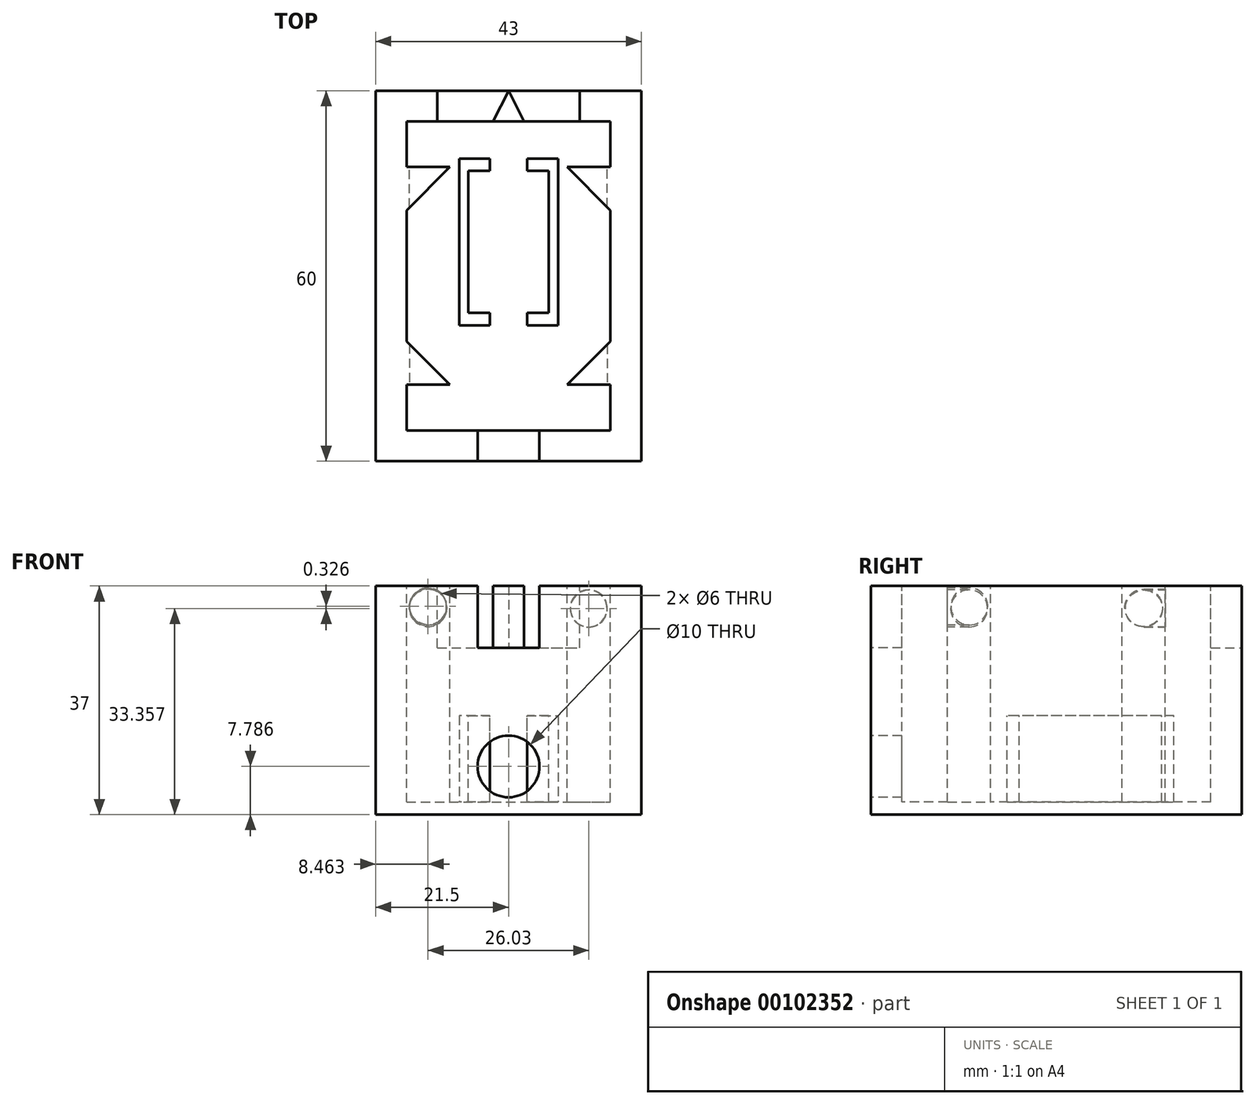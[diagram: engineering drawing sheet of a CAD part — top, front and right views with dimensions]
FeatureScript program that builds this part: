
annotation { "Feature Type Name" : "Feature", "Feature Type Description" : "" }
export const myFeature = defineFeature(function(context is Context, id is Id, definition is map)
    precondition{}
    {
        {
            var Q0;
            Q0=qCreatedBy(makeId("Top.planeOp"),FACE);
            var sketch = newSketch(context, id + "F0", { "sketchPlane" : qUnion([Q0])});
            skLineSegment(sketch, "E0.bottom", {"start": v(-21.5, 30) * mm, "end": v(21.5, 30) * mm});
            skLineSegment(sketch, "E0.top", {"start": v(-21.5, -30) * mm, "end": v(21.5, -30) * mm});
            skLineSegment(sketch, "E0.left", {"start": v(-21.5, 30) * mm, "end": v(-21.5, -30) * mm});
            skLineSegment(sketch, "E0.right", {"start": v(21.5, 30) * mm, "end": v(21.5, -30) * mm});
            skPoint(sketch, "E0.middle", {"position": v(0, 0) * mm});
            skSolve(sketch);
        }
        {
            var Q0;
            Q0=makeQuery(id+"F0.imprint","IMPRINT",FACE,{"disambiguationData":[TD([[makeQuery(id+"F0.imprint","IMPRINT",EDGE,{"derivedFrom":sQuery(id+"F0.wireOp",EDGE,"E0.bottom")}),-1.0]])]});
            extrude(context, id + "F1", {"entities" : qUnion([Q0]), "depth" : 37 * mm});
        }
        {
            var Q0;
            Q0=makeQuery(id+"F1.opExtrude","CAP_FACE",FACE,{"disambiguationData":[OSD([sQuery(id+"F0.wireOp",EDGE,"E0.bottom"),sQuery(id+"F0.wireOp",EDGE,"E0.top"),sQuery(id+"F0.wireOp",EDGE,"E0.left"),sQuery(id+"F0.wireOp",EDGE,"E0.right")])],"isStart":false});
            var sketch = newSketch(context, id + "F2", { "sketchPlane" : qUnion([Q0])});
            skLineSegment(sketch, "E1.bottom", {"start": v(-16.5, 25) * mm, "end": v(16.5, 25) * mm});
            skLineSegment(sketch, "E1.top", {"start": v(-16.5, -25) * mm, "end": v(16.5, -25) * mm});
            skLineSegment(sketch, "E1.left", {"start": v(-16.5, 25) * mm, "end": v(-16.5, -25) * mm});
            skLineSegment(sketch, "E1.right", {"start": v(16.5, 25) * mm, "end": v(16.5, -25) * mm});
            skPoint(sketch, "E1.middle", {"position": v(0, 0) * mm});
            skSolve(sketch);
        }
        {
            var Q0;
            Q0 = qSketchRegion(id + "F2", true);
            extrude(context, id + "F3", {"entities" : qUnion([Q0]), "operationType" : NewBodyOperationType.REMOVE, "oppositeDirection" : true, "depth" : 35 * mm});
        }
        {
            var Q0;
            Q0=makeQuery(id+"F1.opExtrude","CAP_FACE",FACE,{"disambiguationData":[OSD([sQuery(id+"F0.wireOp",EDGE,"E0.bottom"),sQuery(id+"F0.wireOp",EDGE,"E0.top"),sQuery(id+"F0.wireOp",EDGE,"E0.left"),sQuery(id+"F0.wireOp",EDGE,"E0.right")])],"isStart":false});
            var sketch = newSketch(context, id + "F4", { "sketchPlane" : qUnion([Q0])});
            skLineSegment(sketch, "E2", {"start": v(0, 30) * mm, "end": v(-11.5, 30) * mm});
            skLineSegment(sketch, "E3", {"start": v(-11.5, 30) * mm, "end": v(-11.5, 25) * mm});
            skLineSegment(sketch, "E4", {"start": v(-11.5, 25) * mm, "end": v(0, 25) * mm});
            skLineSegment(sketch, "E5", {"start": v(0, 25) * mm, "end": v(11.5, 25) * mm});
            skLineSegment(sketch, "E6", {"start": v(11.5, 25) * mm, "end": v(11.5, 30) * mm});
            skLineSegment(sketch, "E7", {"start": v(11.5, 30) * mm, "end": v(0, 30) * mm});
            skSolve(sketch);
        }
        {
            var Q0;
            Q0 = qSketchRegion(id + "F4", true);
            extrude(context, id + "F5", {"entities" : qUnion([Q0]), "operationType" : NewBodyOperationType.REMOVE, "oppositeDirection" : true, "depth" : 10 * mm});
        }
        {
            var Q0;
            Q0=makeQuery(id+"F5.boolean.opBoolean","COPY",FACE,{"derivedFrom":makeQuery(id+"F5.opExtrude","CAP_FACE",FACE,{"disambiguationData":[OSD([sQuery(id+"F4.wireOp",EDGE,"E2"),sQuery(id+"F4.wireOp",EDGE,"E3"),sQuery(id+"F4.wireOp",EDGE,"E4"),sQuery(id+"F4.wireOp",EDGE,"E5"),sQuery(id+"F4.wireOp",EDGE,"E6"),sQuery(id+"F4.wireOp",EDGE,"E7")])],"isStart":false})});
            var sketch = newSketch(context, id + "F6", { "sketchPlane" : qUnion([Q0])});
            skLineSegment(sketch, "E8", {"start": v(0, 30) * mm, "end": v(-2.5, 25) * mm});
            skLineSegment(sketch, "E9", {"start": v(-2.5, 25) * mm, "end": v(0, 25) * mm});
            skLineSegment(sketch, "E10", {"start": v(0, 25) * mm, "end": v(2.5, 25) * mm});
            skLineSegment(sketch, "E11", {"start": v(2.5, 25) * mm, "end": v(0, 30) * mm});
            skSolve(sketch);
        }
        {
            var Q0;
            Q0=makeQuery(id+"F6.imprint","IMPRINT",FACE,{"disambiguationData":[TD([[makeQuery(id+"F6.imprint","IMPRINT",EDGE,{"derivedFrom":sQuery(id+"F6.wireOp",EDGE,"E8")}),1.0]])]});
            extrude(context, id + "F7", {"entities" : qUnion([Q0]), "operationType" : NewBodyOperationType.ADD, "depth" : 10 * mm});
        }
        {
            var Q0;
            Q0=makeQuery(id+"F1.opExtrude","CAP_FACE",FACE,{"disambiguationData":[OSD([sQuery(id+"F0.wireOp",EDGE,"E0.bottom"),sQuery(id+"F0.wireOp",EDGE,"E0.top"),sQuery(id+"F0.wireOp",EDGE,"E0.left"),sQuery(id+"F0.wireOp",EDGE,"E0.right")])],"isStart":false});
            var sketch = newSketch(context, id + "F8", { "sketchPlane" : qUnion([Q0])});
            skLineSegment(sketch, "E12", {"start": v(0, -25) * mm, "end": v(-5, -25) * mm});
            skLineSegment(sketch, "E13", {"start": v(-5, -25) * mm, "end": v(-5, -30) * mm});
            skLineSegment(sketch, "E14", {"start": v(-5, -30) * mm, "end": v(0, -30) * mm});
            skLineSegment(sketch, "E15", {"start": v(0, -30) * mm, "end": v(5, -30) * mm});
            skLineSegment(sketch, "E16", {"start": v(5, -30) * mm, "end": v(5, -25) * mm});
            skLineSegment(sketch, "E17", {"start": v(5, -25) * mm, "end": v(0, -25) * mm});
            skSolve(sketch);
        }
        {
            var Q0;
            Q0 = qSketchRegion(id + "F8", true);
            extrude(context, id + "F9", {"entities" : qUnion([Q0]), "operationType" : NewBodyOperationType.REMOVE, "oppositeDirection" : true, "depth" : 10 * mm});
        }
        {
            var Q0;
            Q0=makeQuery(id+"F3.boolean.opBoolean","COPY",FACE,{"derivedFrom":makeQuery(id+"F3.opExtrude","CAP_FACE",FACE,{"disambiguationData":[OSD([sQuery(id+"F2.wireOp",EDGE,"E1.bottom"),sQuery(id+"F2.wireOp",EDGE,"E1.top"),sQuery(id+"F2.wireOp",EDGE,"E1.left"),sQuery(id+"F2.wireOp",EDGE,"E1.right")])],"isStart":false})});
            var sketch = newSketch(context, id + "F10", { "sketchPlane" : qUnion([Q0])});
            skSolve(sketch);
        }
        {
            var Q0;
            Q0=makeQuery(id+"F10.imprint","IMPRINT",FACE,{"disambiguationData":[TD([[makeQuery(id+"F10.imprint","IMPRINT",EDGE,{"derivedFrom":makeQuery(id+"F3.boolean.opBoolean","COPY",EDGE,{"derivedFrom":makeQuery(id+"F3.opExtrude","CAP_EDGE",EDGE,{"disambiguationData":[OSD([sQuery(id+"F2.wireOp",EDGE,"E1.bottom")])],"isStart":false})})}),-1.0]])]});
            var sketch = newSketch(context, id + "F11", { "sketchPlane" : qUnion([Q0])});
            skLineSegment(sketch, "E18", {"start": v(0, 19) * mm, "end": v(-8, 19) * mm});
            skLineSegment(sketch, "E19", {"start": v(-8, 19) * mm, "end": v(-8, 0) * mm});
            skLineSegment(sketch, "E20", {"start": v(-8, 0) * mm, "end": v(-8, -8) * mm});
            skLineSegment(sketch, "E21", {"start": v(-8, -8) * mm, "end": v(0, -8) * mm});
            skLineSegment(sketch, "E22", {"start": v(0, -8) * mm, "end": v(8, -8) * mm});
            skLineSegment(sketch, "E23", {"start": v(8, -8) * mm, "end": v(8, 0) * mm});
            skLineSegment(sketch, "E24", {"start": v(8, 0) * mm, "end": v(8, 19) * mm});
            skLineSegment(sketch, "E25", {"start": v(8, 19) * mm, "end": v(0, 19) * mm});
            skSolve(sketch);
        }
        {
            var Q0;
            Q0 = qSketchRegion(id + "F11", true);
            extrude(context, id + "F12", {"entities" : qUnion([Q0]), "operationType" : NewBodyOperationType.ADD, "depth" : 14 * mm});
        }
        {
            var Q0;
            Q0=makeQuery(id+"F12.opExtrude","CAP_FACE",FACE,{"disambiguationData":[OSD([sQuery(id+"F11.wireOp",EDGE,"E18"),sQuery(id+"F11.wireOp",EDGE,"E19"),sQuery(id+"F11.wireOp",EDGE,"E20"),sQuery(id+"F11.wireOp",EDGE,"E21"),sQuery(id+"F11.wireOp",EDGE,"E22"),sQuery(id+"F11.wireOp",EDGE,"E23"),sQuery(id+"F11.wireOp",EDGE,"E24"),sQuery(id+"F11.wireOp",EDGE,"E25")])],"isStart":false});
            var sketch = newSketch(context, id + "F13", { "sketchPlane" : qUnion([Q0])});
            skLineSegment(sketch, "E26", {"start": v(0, 17) * mm, "end": v(-6.5, 17) * mm});
            skLineSegment(sketch, "E27", {"start": v(-6.5, 17) * mm, "end": v(-6.5, 0) * mm});
            skLineSegment(sketch, "E28", {"start": v(-6.5, 0) * mm, "end": v(-6.5, -6) * mm});
            skLineSegment(sketch, "E29", {"start": v(-6.5, -6) * mm, "end": v(0, -6) * mm});
            skLineSegment(sketch, "E30", {"start": v(0, -6) * mm, "end": v(6.5, -6) * mm});
            skLineSegment(sketch, "E31", {"start": v(6.5, -6) * mm, "end": v(6.5, 0) * mm});
            skLineSegment(sketch, "E32", {"start": v(6.5, 0) * mm, "end": v(6.5, 17) * mm});
            skLineSegment(sketch, "E33", {"start": v(6.5, 17) * mm, "end": v(0, 17) * mm});
            skSolve(sketch);
        }
        {
            var Q0;
            Q0 = qSketchRegion(id + "F13", true);
            extrude(context, id + "F14", {"entities" : qUnion([Q0]), "operationType" : NewBodyOperationType.REMOVE, "oppositeDirection" : true, "depth" : 14 * mm});
        }
        {
            var Q0;
            Q0=makeQuery(id+"F12.opExtrude","CAP_FACE",FACE,{"disambiguationData":[OSD([sQuery(id+"F11.wireOp",EDGE,"E18"),sQuery(id+"F11.wireOp",EDGE,"E19"),sQuery(id+"F11.wireOp",EDGE,"E20"),sQuery(id+"F11.wireOp",EDGE,"E21"),sQuery(id+"F11.wireOp",EDGE,"E22"),sQuery(id+"F11.wireOp",EDGE,"E23"),sQuery(id+"F11.wireOp",EDGE,"E24"),sQuery(id+"F11.wireOp",EDGE,"E25")])],"isStart":false});
            var sketch = newSketch(context, id + "F15", { "sketchPlane" : qUnion([Q0])});
            skLineSegment(sketch, "E34", {"start": v(0, 19) * mm, "end": v(-3, 19) * mm});
            skLineSegment(sketch, "E35", {"start": v(-3, 19) * mm, "end": v(-3, 17) * mm});
            skLineSegment(sketch, "E36", {"start": v(-3, 17) * mm, "end": v(0, 17) * mm});
            skLineSegment(sketch, "E37", {"start": v(0, 17) * mm, "end": v(3, 17) * mm});
            skLineSegment(sketch, "E38", {"start": v(3, 17) * mm, "end": v(3, 19) * mm});
            skLineSegment(sketch, "E39", {"start": v(3, 19) * mm, "end": v(0, 19) * mm});
            skSolve(sketch);
        }
        {
            var Q0;
            Q0 = qSketchRegion(id + "F15", true);
            extrude(context, id + "F16", {"entities" : qUnion([Q0]), "operationType" : NewBodyOperationType.REMOVE, "oppositeDirection" : true, "depth" : 14 * mm});
        }
        {
            var Q0;
            Q0=makeQuery(id+"F12.opExtrude","CAP_FACE",FACE,{"disambiguationData":[OSD([sQuery(id+"F11.wireOp",EDGE,"E18"),sQuery(id+"F11.wireOp",EDGE,"E19"),sQuery(id+"F11.wireOp",EDGE,"E20"),sQuery(id+"F11.wireOp",EDGE,"E21"),sQuery(id+"F11.wireOp",EDGE,"E22"),sQuery(id+"F11.wireOp",EDGE,"E23"),sQuery(id+"F11.wireOp",EDGE,"E24"),sQuery(id+"F11.wireOp",EDGE,"E25")])],"isStart":false});
            var sketch = newSketch(context, id + "F17", { "sketchPlane" : qUnion([Q0])});
            skLineSegment(sketch, "E40", {"start": v(0, -6) * mm, "end": v(-3, -6) * mm});
            skLineSegment(sketch, "E41", {"start": v(-3, -6) * mm, "end": v(-3, -8) * mm});
            skLineSegment(sketch, "E42", {"start": v(-3, -8) * mm, "end": v(0, -8) * mm});
            skLineSegment(sketch, "E43", {"start": v(0, -8) * mm, "end": v(3, -8) * mm});
            skLineSegment(sketch, "E44", {"start": v(3, -8) * mm, "end": v(3, -6) * mm});
            skLineSegment(sketch, "E45", {"start": v(3, -6) * mm, "end": v(0, -6) * mm});
            skSolve(sketch);
        }
        {
            var Q0;
            Q0 = qSketchRegion(id + "F17", true);
            extrude(context, id + "F18", {"entities" : qUnion([Q0]), "operationType" : NewBodyOperationType.REMOVE, "oppositeDirection" : true, "depth" : 14 * mm});
        }
        {
            var Q0;
            Q0=makeQuery(id+"F1.opExtrude","SWEPT_FACE",FACE,{"disambiguationData":[OSD([sQuery(id+"F0.wireOp",EDGE,"E0.top")])]});
            var sketch = newSketch(context, id + "F19", { "sketchPlane" : qUnion([Q0])});
            skCircle(sketch, "E46", {"center": v(0, 7.79) * mm, "radius": 5 * mm});
            skSolve(sketch);
        }
        {
            var Q0;
            Q0 = qSketchRegion(id + "F19", true);
            extrude(context, id + "F20", {"entities" : qUnion([Q0]), "operationType" : NewBodyOperationType.REMOVE, "oppositeDirection" : true, "depth" : 6 * mm});
        }
        {
            var Q0;
            {var subQ0=sQuery(id+"F0.wireOp",EDGE,"E0.left");var subQ1=sQuery(id+"F0.wireOp",EDGE,"E0.top");var subQ2=sQuery(id+"F0.wireOp",EDGE,"E0.bottom");Q0=makeQuery(id+"F9.boolean.opBoolean","SPLIT",FACE,{"disambiguationData":[TD([makeQuery(id+"F1.opExtrude","SWEPT_FACE",FACE,{"disambiguationData":[OSD([subQ0])]})])],"derivedFrom":makeQuery(id+"F1.opExtrude","CAP_FACE",FACE,{"disambiguationData":[OSD([subQ2,subQ1,subQ0,sQuery(id+"F0.wireOp",EDGE,"E0.right")])],"isStart":false})});}
            var sketch = newSketch(context, id + "F21", { "sketchPlane" : qUnion([Q0])});
            skLineSegment(sketch, "E47", {"start": v(-16.5, -17.62) * mm, "end": v(-9.5, -17.62) * mm});
            skLineSegment(sketch, "E48", {"start": v(-9.5, -17.62) * mm, "end": v(-16.5, -10.62) * mm});
            skLineSegment(sketch, "E49", {"start": v(-16.5, -10.62) * mm, "end": v(-16.5, -17.62) * mm});
            skLineSegment(sketch, "E50.MirrorCS", {"start": v(16.5, -10.62) * mm, "end": v(16.5, -17.62) * mm});
            skLineSegment(sketch, "E51.MirrorCS", {"start": v(9.5, -17.62) * mm, "end": v(16.5, -10.62) * mm});
            skLineSegment(sketch, "E52.MirrorCS", {"start": v(16.5, -17.62) * mm, "end": v(9.5, -17.62) * mm});
            skLineSegment(sketch, "E53.MirrorCS", {"start": v(-16.5, 17.62) * mm, "end": v(-9.5, 17.62) * mm});
            skLineSegment(sketch, "E54.MirrorCS", {"start": v(-16.5, 10.62) * mm, "end": v(-16.5, 17.62) * mm});
            skLineSegment(sketch, "E55.MirrorCS", {"start": v(-9.5, 17.62) * mm, "end": v(-16.5, 10.62) * mm});
            skLineSegment(sketch, "E56.MirrorCS", {"start": v(16.5, 10.62) * mm, "end": v(16.5, 17.62) * mm});
            skLineSegment(sketch, "E57.MirrorCS", {"start": v(16.5, 17.62) * mm, "end": v(9.5, 17.62) * mm});
            skLineSegment(sketch, "E58.MirrorCS", {"start": v(9.5, 17.62) * mm, "end": v(16.5, 10.62) * mm});
            skSolve(sketch);
        }
        {
            var Q0;
            Q0=makeQuery(id+"F21.imprint","IMPRINT",FACE,{"disambiguationData":[TD([[makeQuery(id+"F21.imprint","IMPRINT",EDGE,{"derivedFrom":sQuery(id+"F21.wireOp",EDGE,"E47")}),1.0]])]});
            extrude(context, id + "F22", {"entities" : qUnion([Q0]), "operationType" : NewBodyOperationType.ADD, "oppositeDirection" : true, "depth" : 33 * mm});
        }
        {
            var Q0;
            Q0=makeQuery(id+"F21.imprint","IMPRINT",FACE,{"disambiguationData":[TD([[makeQuery(id+"F21.imprint","IMPRINT",EDGE,{"derivedFrom":sQuery(id+"F21.wireOp",EDGE,"E50.MirrorCS")}),-1.0]])]});
            extrude(context, id + "F23", {"entities" : qUnion([Q0]), "operationType" : NewBodyOperationType.ADD, "oppositeDirection" : true, "depth" : 33 * mm});
        }
        {
            var Q0;
            Q0=makeQuery(id+"F21.imprint","IMPRINT",FACE,{"disambiguationData":[TD([[makeQuery(id+"F21.imprint","IMPRINT",EDGE,{"derivedFrom":sQuery(id+"F21.wireOp",EDGE,"E53.MirrorCS")}),-1.0]])]});
            extrude(context, id + "F24", {"entities" : qUnion([Q0]), "operationType" : NewBodyOperationType.ADD, "oppositeDirection" : true, "depth" : 33 * mm});
        }
        {
            var Q0;
            Q0=makeQuery(id+"F21.imprint","IMPRINT",FACE,{"disambiguationData":[TD([[makeQuery(id+"F21.imprint","IMPRINT",EDGE,{"derivedFrom":sQuery(id+"F21.wireOp",EDGE,"E56.MirrorCS")}),1.0]])]});
            extrude(context, id + "F25", {"entities" : qUnion([Q0]), "operationType" : NewBodyOperationType.ADD, "oppositeDirection" : true, "depth" : 33 * mm});
        }
        {
            var Q0;
            Q0=makeQuery(id+"F22.opExtrude","SWEPT_FACE",FACE,{"disambiguationData":[OSD([sQuery(id+"F21.wireOp",EDGE,"E47")])]});
            var sketch = newSketch(context, id + "F26", { "sketchPlane" : qUnion([Q0])});
            skCircle(sketch, "E59", {"center": v(-13, 32.92) * mm, "radius": 3 * mm});
            skPoint(sketch, "E59.first.point", {"position": v(-13, 35.92) * mm});
            skPoint(sketch, "E59.first.point.positionSnap0", {"position": v(-13, 37) * mm});
            skPoint(sketch, "E59.second.point", {"position": v(-13, 29.92) * mm});
            skPoint(sketch, "E59.second.point.positionSnap0", {"position": v(-13, 37) * mm});
            skPoint(sketch, "E59.third.point", {"position": v(-10, 33.05) * mm});
            skSolve(sketch);
        }
        {
            var Q0;
            Q0 = qSketchRegion(id + "F26", true);
            extrude(context, id + "F27", {"entities" : qUnion([Q0]), "operationType" : NewBodyOperationType.REMOVE, "oppositeDirection" : true, "depth" : 15 * mm});
        }
        {
            var Q0;
            Q0=makeQuery(id+"F23.opExtrude","SWEPT_FACE",FACE,{"disambiguationData":[OSD([sQuery(id+"F21.wireOp",EDGE,"E52.MirrorCS")])]});
            var sketch = newSketch(context, id + "F28", { "sketchPlane" : qUnion([Q0])});
            skCircle(sketch, "E60", {"center": v(13.05, 32.74) * mm, "radius": 3.03 * mm});
            skPoint(sketch, "E60.first.point", {"position": v(13, 35.76) * mm});
            skPoint(sketch, "E60.first.point.positionSnap0", {"position": v(13, 37) * mm});
            skPoint(sketch, "E60.second.point", {"position": v(13, 29.71) * mm});
            skPoint(sketch, "E60.second.point.positionSnap0", {"position": v(13, 37) * mm});
            skPoint(sketch, "E60.third.point", {"position": v(10.05, 33.13) * mm});
            skSolve(sketch);
        }
        {
            var Q0;
            Q0 = qSketchRegion(id + "F28", true);
            extrude(context, id + "F29", {"entities" : qUnion([Q0]), "operationType" : NewBodyOperationType.REMOVE, "oppositeDirection" : true, "depth" : 15 * mm});
        }
        {
            var Q0;
            Q0=makeQuery(id+"F25.opExtrude","SWEPT_FACE",FACE,{"disambiguationData":[OSD([sQuery(id+"F21.wireOp",EDGE,"E57.MirrorCS")])]});
            var sketch = newSketch(context, id + "F30", { "sketchPlane" : qUnion([Q0])});
            skCircle(sketch, "E61", {"center": v(-12.98, 32.83) * mm, "radius": 3 * mm});
            skPoint(sketch, "E61.first.point", {"position": v(-13, 35.83) * mm});
            skPoint(sketch, "E61.first.point.positionSnap0", {"position": v(-13, 37) * mm});
            skPoint(sketch, "E61.second.point", {"position": v(-13, 29.83) * mm});
            skPoint(sketch, "E61.second.point.positionSnap0", {"position": v(-13, 37) * mm});
            skPoint(sketch, "E61.third.point", {"position": v(-10.03, 32.28) * mm});
            skSolve(sketch);
        }
        {
            var Q0;
            Q0 = qSketchRegion(id + "F30", true);
            extrude(context, id + "F31", {"entities" : qUnion([Q0]), "operationType" : NewBodyOperationType.REMOVE, "oppositeDirection" : true, "depth" : 15 * mm});
        }
        {
            var Q0;
            Q0=makeQuery(id+"F24.opExtrude","SWEPT_FACE",FACE,{"disambiguationData":[OSD([sQuery(id+"F21.wireOp",EDGE,"E53.MirrorCS")])]});
            var sketch = newSketch(context, id + "F32", { "sketchPlane" : qUnion([Q0])});
            skCircle(sketch, "E62", {"center": v(13.3, 33.35) * mm, "radius": 3 * mm});
            skPoint(sketch, "E62.first.point", {"position": v(13, 36.33) * mm});
            skPoint(sketch, "E62.first.point.positionSnap0", {"position": v(13, 37) * mm});
            skPoint(sketch, "E62.second.point", {"position": v(13, 30.36) * mm});
            skPoint(sketch, "E62.second.point.positionSnap0", {"position": v(13, 37) * mm});
            skPoint(sketch, "E62.third.point", {"position": v(10.34, 33.83) * mm});
            skSolve(sketch);
        }
        {
            var Q0;
            Q0 = qSketchRegion(id + "F32", true);
            extrude(context, id + "F33", {"entities" : qUnion([Q0]), "operationType" : NewBodyOperationType.REMOVE, "oppositeDirection" : true, "depth" : 15 * mm});
        }
        {
            var Q0;
            Q0 = qSketchRegion(id + "F21", true);
            extrude(context, id + "F34", {"entities" : qUnion([Q0]), "operationType" : NewBodyOperationType.ADD, "oppositeDirection" : true, "depth" : 35 * mm});
        }
        {
            var Q0;
            {var subQ0=sQuery(id+"F21.wireOp",EDGE,"E47");Q0=makeQuery(id+"F34.boolean.opBoolean","MERGE",FACE,{"derivedFrom":[makeQuery(id+"F22.opExtrude","SWEPT_FACE",FACE,{"disambiguationData":[OSD([subQ0])]}),makeQuery(id+"F34.opExtrude","SWEPT_FACE",FACE,{"disambiguationData":[OSD([subQ0])]})]});}
            var sketch = newSketch(context, id + "F35", { "sketchPlane" : qUnion([Q0])});
            skCircle(sketch, "E63", {"center": v(-13.04, 33.68) * mm, "radius": 3 * mm});
            skPoint(sketch, "E63.first.point", {"position": v(-13, 36.68) * mm});
            skPoint(sketch, "E63.first.point.positionSnap0", {"position": v(-13, 37) * mm});
            skPoint(sketch, "E63.second.point", {"position": v(-13, 30.68) * mm});
            skPoint(sketch, "E63.second.point.positionSnap0", {"position": v(-13, 37) * mm});
            skPoint(sketch, "E63.third.point", {"position": v(-10.04, 33.77) * mm});
            skSolve(sketch);
        }
        {
            var Q0;
            Q0 = qSketchRegion(id + "F35", true);
            extrude(context, id + "F36", {"entities" : qUnion([Q0]), "operationType" : NewBodyOperationType.REMOVE, "oppositeDirection" : true, "depth" : 10 * mm});
        }
        {
            var Q0;
            {var subQ0=sQuery(id+"F21.wireOp",EDGE,"E52.MirrorCS");Q0=makeQuery(id+"F34.boolean.opBoolean","MERGE",FACE,{"derivedFrom":[makeQuery(id+"F23.opExtrude","SWEPT_FACE",FACE,{"disambiguationData":[OSD([subQ0])]}),makeQuery(id+"F34.opExtrude","SWEPT_FACE",FACE,{"disambiguationData":[OSD([subQ0])]})]});}
            var sketch = newSketch(context, id + "F37", { "sketchPlane" : qUnion([Q0])});
            skCircle(sketch, "E64", {"center": v(13, 33.36) * mm, "radius": 3 * mm});
            skPoint(sketch, "E64.first.point", {"position": v(13, 36.36) * mm});
            skPoint(sketch, "E64.first.point.positionSnap0", {"position": v(13, 37) * mm});
            skPoint(sketch, "E64.second.point", {"position": v(13, 30.36) * mm});
            skPoint(sketch, "E64.second.point.positionSnap0", {"position": v(13, 37) * mm});
            skPoint(sketch, "E64.third.point", {"position": v(10, 33.35) * mm});
            skSolve(sketch);
        }
        {
            var Q0;
            Q0 = qSketchRegion(id + "F37", true);
            extrude(context, id + "F38", {"entities" : qUnion([Q0]), "operationType" : NewBodyOperationType.REMOVE, "oppositeDirection" : true, "depth" : 10 * mm});
        }
        {
            var Q0;
            {var subQ0=sQuery(id+"F21.wireOp",EDGE,"E57.MirrorCS");Q0=makeQuery(id+"F34.boolean.opBoolean","MERGE",FACE,{"derivedFrom":[makeQuery(id+"F25.opExtrude","SWEPT_FACE",FACE,{"disambiguationData":[OSD([subQ0])]}),makeQuery(id+"F34.opExtrude","SWEPT_FACE",FACE,{"disambiguationData":[OSD([subQ0])]})]});}
            var sketch = newSketch(context, id + "F39", { "sketchPlane" : qUnion([Q0])});
            skCircle(sketch, "E65", {"center": v(-12.97, 33.34) * mm, "radius": 3 * mm});
            skPoint(sketch, "E65.first.point", {"position": v(-13, 36.35) * mm});
            skPoint(sketch, "E65.first.point.positionSnap0", {"position": v(-13, 37) * mm});
            skPoint(sketch, "E65.second.point", {"position": v(-13, 30.34) * mm});
            skPoint(sketch, "E65.second.point.positionSnap0", {"position": v(-13, 37) * mm});
            skPoint(sketch, "E65.third.point", {"position": v(-9.97, 33.19) * mm});
            skSolve(sketch);
        }
        {
            var Q0;
            Q0 = qSketchRegion(id + "F39", true);
            extrude(context, id + "F40", {"entities" : qUnion([Q0]), "operationType" : NewBodyOperationType.REMOVE, "oppositeDirection" : true, "depth" : 10 * mm});
        }
        {
            var Q0;
            {var subQ0=sQuery(id+"F21.wireOp",EDGE,"E53.MirrorCS");Q0=makeQuery(id+"F34.boolean.opBoolean","MERGE",FACE,{"derivedFrom":[makeQuery(id+"F24.opExtrude","SWEPT_FACE",FACE,{"disambiguationData":[OSD([subQ0])]}),makeQuery(id+"F34.opExtrude","SWEPT_FACE",FACE,{"disambiguationData":[OSD([subQ0])]})]});}
            var sketch = newSketch(context, id + "F41", { "sketchPlane" : qUnion([Q0])});
            skCircle(sketch, "E66", {"center": v(13.02, 33.46) * mm, "radius": 3.04 * mm});
            skPoint(sketch, "E66.first.point", {"position": v(13, 36.5) * mm});
            skPoint(sketch, "E66.first.point.positionSnap0", {"position": v(13, 37) * mm});
            skPoint(sketch, "E66.second.point", {"position": v(13, 30.42) * mm});
            skPoint(sketch, "E66.second.point.positionSnap0", {"position": v(13, 37) * mm});
            skPoint(sketch, "E66.third.point", {"position": v(10.02, 32.97) * mm});
            skSolve(sketch);
        }
        {
            var Q0;
            Q0 = qSketchRegion(id + "F41", true);
            extrude(context, id + "F42", {"entities" : qUnion([Q0]), "operationType" : NewBodyOperationType.REMOVE, "oppositeDirection" : true, "depth" : 10 * mm});
        }
    });
